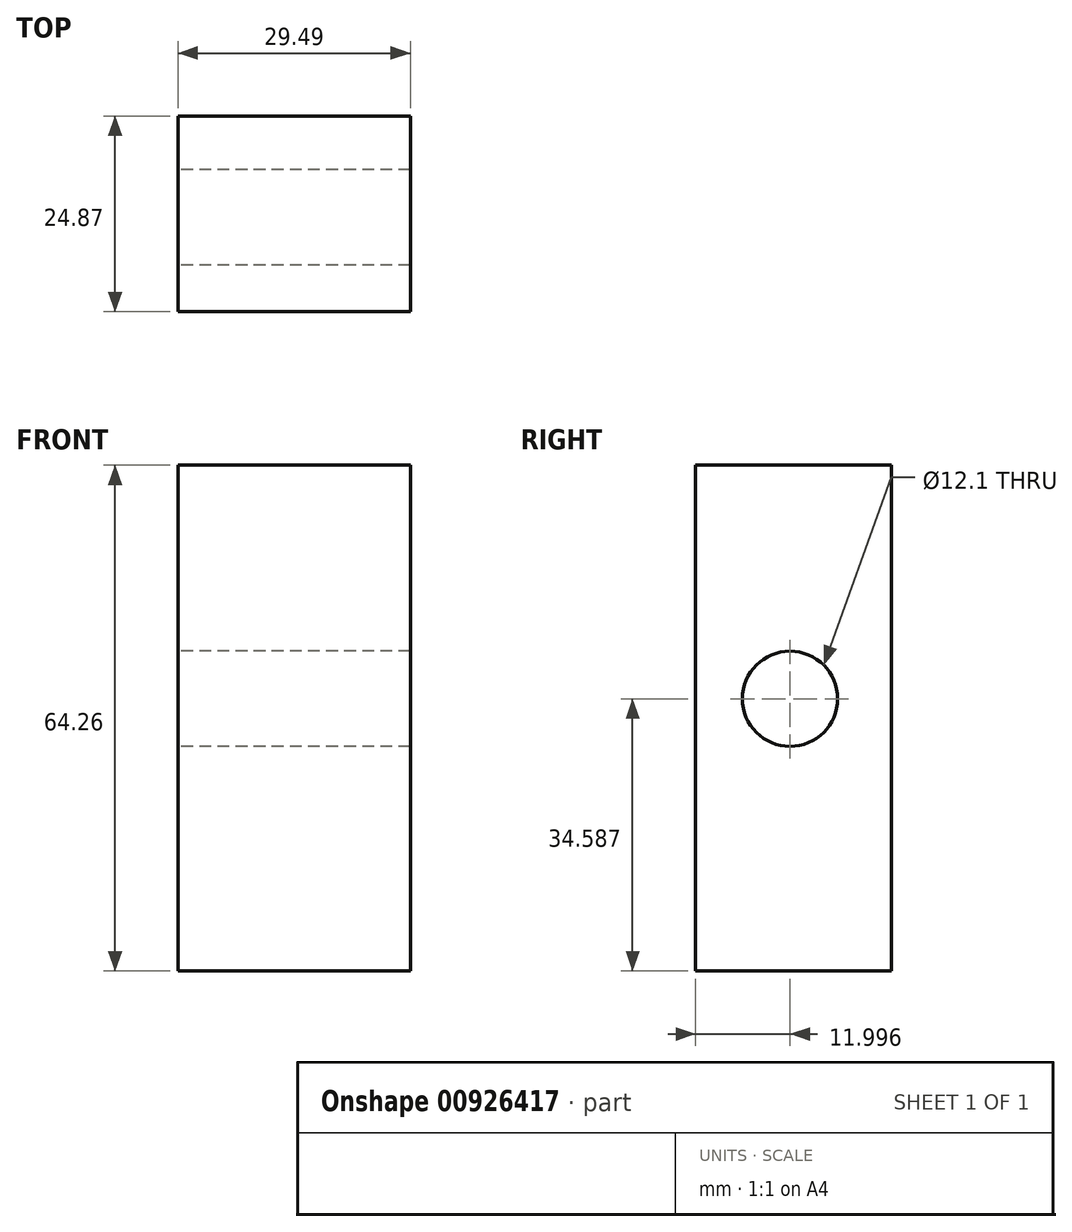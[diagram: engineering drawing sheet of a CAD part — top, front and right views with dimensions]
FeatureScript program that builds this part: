
annotation { "Feature Type Name" : "Feature", "Feature Type Description" : "" }
export const myFeature = defineFeature(function(context is Context, id is Id, definition is map)
    precondition{}
    {
        {
            var Q0;
            Q0=qCreatedBy(makeId("Top.planeOp"),FACE);
            var sketch = newSketch(context, id + "F0", { "sketchPlane" : qUnion([Q0])});
            skLineSegment(sketch, "E0.bottom", {"start": v(-29.49, 28.93) * mm, "end": v(0, 28.93) * mm});
            skLineSegment(sketch, "E0.top", {"start": v(-29.49, 4.06) * mm, "end": v(0, 4.06) * mm});
            skLineSegment(sketch, "E0.left", {"start": v(-29.49, 28.93) * mm, "end": v(-29.49, 4.06) * mm});
            skLineSegment(sketch, "E0.right", {"start": v(0, 28.93) * mm, "end": v(0, 4.06) * mm});
            skSolve(sketch);
        }
        {
            var Q0;
            Q0 = qSketchRegion(id + "F0", true);
            extrude(context, id + "F1", {"entities" : qUnion([Q0]), "depth" : 64.26 * mm, "offsetDistance" : 25.4 * mm});
        }
        {
            var Q0;
            Q0=makeQuery(id+"F1.opExtrude","SWEPT_FACE",FACE,{"disambiguationData":[OSD([sQuery(id+"F0.wireOp",EDGE,"E0.left")])]});
            var sketch = newSketch(context, id + "F2", { "sketchPlane" : qUnion([Q0])});
            skCircle(sketch, "E1", {"center": v(-16.06, 34.59) * mm, "radius": 6.05 * mm});
            skSolve(sketch);
        }
        {
            var Q0;
            Q0=makeQuery(id+"F2.imprint","IMPRINT",FACE,{"disambiguationData":[TD([[makeQuery(id+"F2.imprint","IMPRINT",EDGE,{"derivedFrom":sQuery(id+"F2.wireOp",EDGE,"E1")}),1.0]])]});
            var Q1;
            Q1=makeQuery(id+"F1.opExtrude","SWEPT_FACE",FACE,{"disambiguationData":[OSD([sQuery(id+"F0.wireOp",EDGE,"E0.right")])]});
            extrude(context, id + "F3", {"entities" : qUnion([Q0, Q1]), "operationType" : NewBodyOperationType.REMOVE, "oppositeDirection" : true, "depth" : 36.32 * mm, "offsetDistance" : 25.4 * mm});
        }
    });
